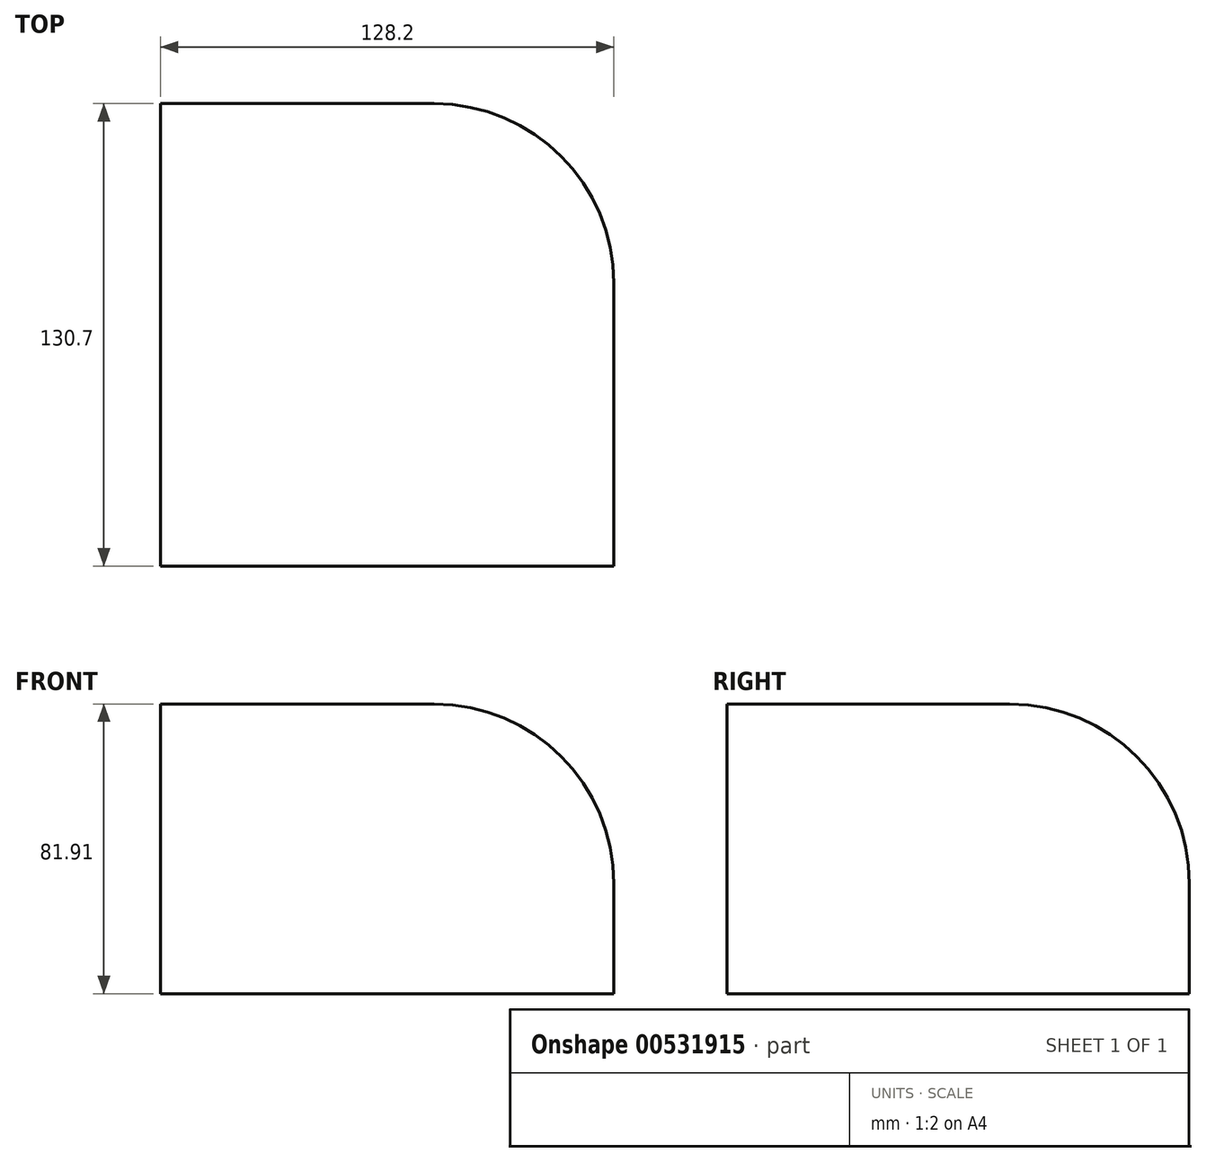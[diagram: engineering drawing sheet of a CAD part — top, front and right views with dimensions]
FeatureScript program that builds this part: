
annotation { "Feature Type Name" : "Feature", "Feature Type Description" : "" }
export const myFeature = defineFeature(function(context is Context, id is Id, definition is map)
    precondition{}
    {
        {
            var Q0;
            Q0=qCreatedBy(makeId("Top.planeOp"),FACE);
            var sketch = newSketch(context, id + "F0", { "sketchPlane" : qUnion([Q0])});
            skLineSegment(sketch, "E0.bottom", {"start": v(-64.1, -65.35) * mm, "end": v(64.1, -65.35) * mm});
            skLineSegment(sketch, "E0.top", {"start": v(-64.1, 65.35) * mm, "end": v(64.1, 65.35) * mm});
            skLineSegment(sketch, "E0.left", {"start": v(-64.1, -65.35) * mm, "end": v(-64.1, 65.35) * mm});
            skLineSegment(sketch, "E0.right", {"start": v(64.1, -65.35) * mm, "end": v(64.1, 65.35) * mm});
            skPoint(sketch, "E0.middle", {"position": v(0, 0) * mm});
            skSolve(sketch);
        }
        {
            var Q0;
            Q0=makeQuery(id+"F0.imprint","IMPRINT",FACE,{"disambiguationData":[TD([[makeQuery(id+"F0.imprint","IMPRINT",EDGE,{"derivedFrom":sQuery(id+"F0.wireOp",EDGE,"E0.bottom")}),1.0]])]});
            extrude(context, id + "F1", {"entities" : qUnion([Q0]), "depth" : 81.9 * mm, "offsetDistance" : 25.4 * mm});
        }
        {
            var Q0;
            Q0=makeQuery(id+"F1.opExtrude","CAP_EDGE",EDGE,{"disambiguationData":[OSD([sQuery(id+"F0.wireOp",EDGE,"E0.top")])],"isStart":false});
            var Q1;
            Q1=makeQuery(id+"F1.opExtrude","CAP_EDGE",EDGE,{"disambiguationData":[OSD([sQuery(id+"F0.wireOp",EDGE,"E0.right")])],"isStart":false});
            var Q2;
            Q2=makeQuery(id+"F1.opExtrude","SWEPT_EDGE",EDGE,{"disambiguationData":[OSD([sQuery(id+"F0.wireOp",EDGE,"E0.top"),sQuery(id+"F0.wireOp",EDGE,"E0.right")])]});
            fillet(context, id + "F2", {"entities" : qUnion([Q0, Q1, Q2]), "radius" : 50.8 * mm, "tangentPropagation" : true, "allowEdgeOverflow" : false});
        }
    });
